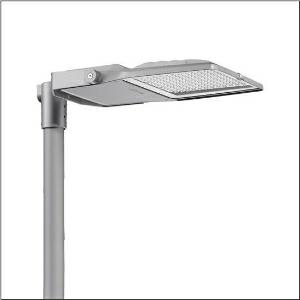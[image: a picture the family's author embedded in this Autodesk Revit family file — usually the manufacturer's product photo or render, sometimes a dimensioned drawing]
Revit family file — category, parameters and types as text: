
# Revit family: floodlight_fl_21_midi___pl52_5xa7786f2d3a_9b56
name_source: partatom
category: Lighting Fixtures
units: mm (PartAtom-declared; Revit-internal decimal feet)

## family parameters
Cut with Voids When Loaded = No
Host = Face
Light Source = No
Part Type = Normal
Room Calculation Point = No
Round Connector Dimension = Use Diameter
Shared = No

## types (1)
- --- (1 x LED, 35750 lm, 271.6 W, 3000K)
    Apparent Load = 272 VA
    CIE Flux Codes = 26 60 98 100 100
    Color Rendering = 70
    Color Temperature = 3000K
    Default Elevation = 1800 mm
    Description = Floodlight FL 21 midi, floodlight, primary light control with lens, of PMMA, primary optical cover: protective disc, of toughened safety glass, transparent, light distribution: PL52, light emission: direct distribution, installation type: surface-mounted, LED, High Power LED, rated luminous flux: 35.750lm, luminous efficacy: 132lm/W, light colour: 730, colour temperature: 3000K, control gear: Smart Interface (Zhaga), control: flexible luminous flux parameterisation, time-dependent luminous flux control, constant luminous flux control, overheat protection, pre-setting: logarithmic dimming characteristic, with terminal, 6-pole, mains connection: 220..240V, AC, 50/60Hz, start of lifetime: 272W, end of service life: 287W, reduction: 123W, luminaire housing, of diecast aluminium, powder-coated, Siteco® metallic grey (DB 702S), corrosivity category C5 mid according to DIN EN ISO 12944, suitable for swimming pools, chlorine-resistant, sealing non-destructively replaceable, please order mast flange separately, mast bracket, of steel, galvanised, powder-coated, Siteco® metallic grey (DB 702S), Smart Interface below and above, protection rating (complete): IP66, insulation class (complete): insulation class II (safety insulation), certification: CE, ENEC, VDE, protection symbol: D, impact resistance: IK08, permissible operating ambient temperature: -40..+40°C, permissible operating ambient temperature for outdoor applications: -40..+50°C, standard: DIN EN 12944, LABS conformity tested according to VDMA 24364:2018-05, packaging unit: 1 piece

Light Distribution: PL52
    Height = 76 mm
    Lamp = 1 x LED
    Lamp Light Flux = 35750 lm
    Lamp Power = 271.6 W
    Lamp count = 1
    Length = 657 mm
    Luminous efficacy = 132 lm/W
    Manufacturer = Siteco
    ModVariant = No
    Model = 5XA7786F2D3A
    Number of Poles = 1
    OnlyDefault = Yes
    Power Factor = 1
    Product Name = Floodlight FL 21 midi | PL52
    Product group = floodlight | pylon annexe
    ProductGroupID = 6200
    Protection Class = Protection class II
    Protection Degree = IP 66
    RLX_Detail_Level = 1
    RLX_Emergency_Light_Flux = 0 lm
    RLX_Emergency_Type = 0
    RLX_Emergency_Type_DB = No
    RlxData = <blob elided: 153845 chars, md5=e0a0b509>
    Socket = socket
    Standby Power = 0 W
    System Light Flux = 35750 lm
    System Power = 272 W
    Type Comments = factory setting: luminous flux: 100 % | dim-lin: 254 | 620 mA
    Type Image = l_1007123.jpg
    URL = http://relux.com
    VarID = @adj_177402
    Voltage = 0 V
    Weight = 0.00 kg
    Width = 442 mm

## geometry (parser evidence)
native form markers: Blend x4, Sweep x14
no freeform markers — native parametric forms only
